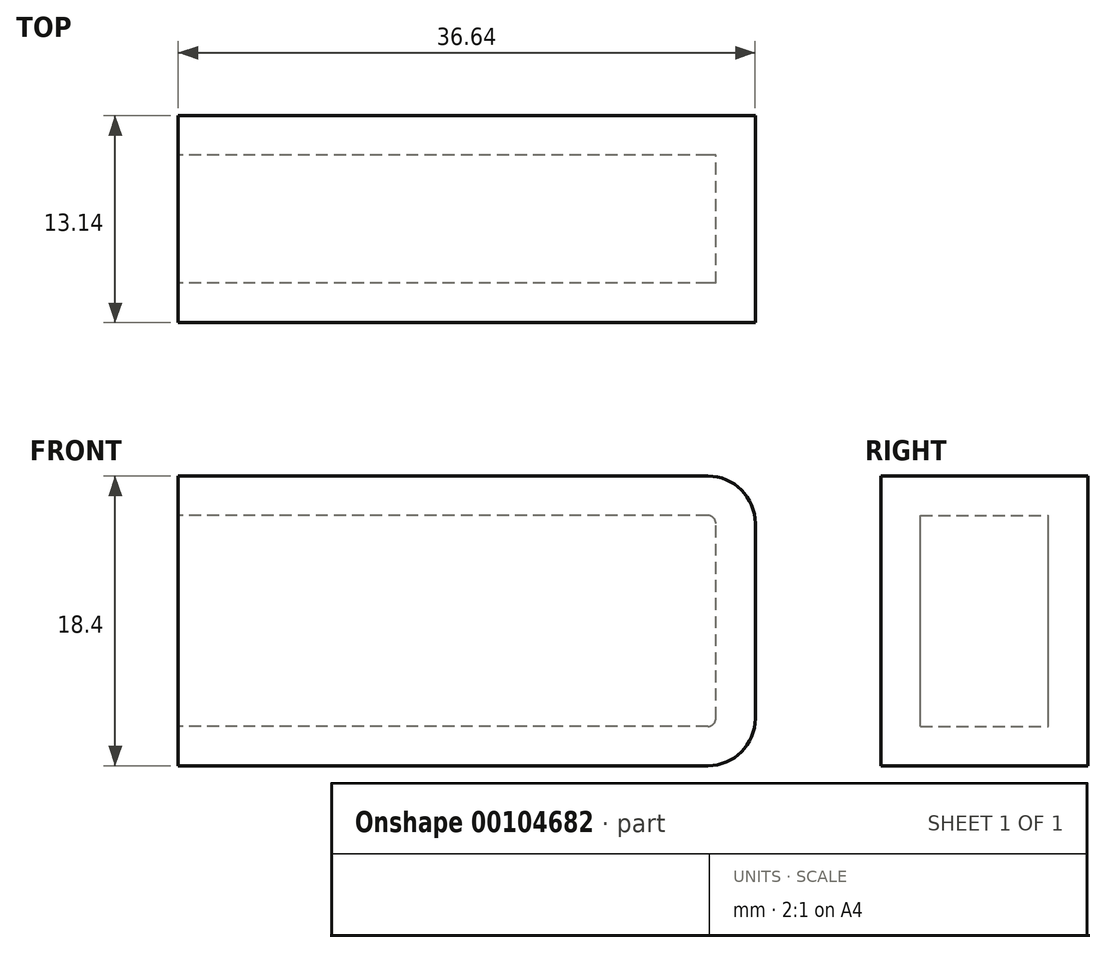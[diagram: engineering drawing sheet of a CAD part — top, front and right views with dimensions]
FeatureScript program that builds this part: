
annotation { "Feature Type Name" : "Feature", "Feature Type Description" : "" }
export const myFeature = defineFeature(function(context is Context, id is Id, definition is map)
    precondition{}
    {
        {
            var Q0;
            Q0=qCreatedBy(makeId("Front.planeOp"),FACE);
            var sketch = newSketch(context, id + "F0", { "sketchPlane" : qUnion([Q0])});
            skLineSegment(sketch, "E0.bottom", {"start": v(15.33, -9.2) * mm, "end": v(-18.32, -9.2) * mm});
            skLineSegment(sketch, "E0.top", {"start": v(15.33, 9.2) * mm, "end": v(-18.32, 9.2) * mm});
            skLineSegment(sketch, "E0.left", {"start": v(18.32, -6.2) * mm, "end": v(18.32, 6.2) * mm});
            skLineSegment(sketch, "E0.right", {"start": v(-18.32, -9.2) * mm, "end": v(-18.32, 9.2) * mm});
            skPoint(sketch, "E0.middle", {"position": v(0, 0) * mm});
            skPoint(sketch, "E1.visualSharp", {"position": v(18.32, 9.2) * mm});
            skArc(sketch, "E1.filletArc", {"start": v(18.32, 6.2) * mm, "mid": v(17.45, 8.32) * mm, "end": v(15.33, 9.2) * mm});
            skPoint(sketch, "E2.visualSharp", {"position": v(18.32, -9.2) * mm});
            skArc(sketch, "E2.filletArc", {"start": v(15.33, -9.2) * mm, "mid": v(17.45, -8.32) * mm, "end": v(18.32, -6.2) * mm});
            skSolve(sketch);
        }
        {
            var Q0;
            Q0=makeQuery(id+"F0.imprint","IMPRINT",FACE,{"disambiguationData":[TD([[makeQuery(id+"F0.imprint","IMPRINT",EDGE,{"derivedFrom":sQuery(id+"F0.wireOp",EDGE,"E0.bottom")}),-1.0]])]});
            extrude(context, id + "F1", {"entities" : qUnion([Q0]), "depth" : (8.14 + 5) * mm});
        }
        {
            var Q0;
            Q0=makeQuery(id+"F1.opExtrude","SWEPT_FACE",FACE,{"disambiguationData":[OSD([sQuery(id+"F0.wireOp",EDGE,"E0.right")])]});
            shell(context, id + "F2", {"entities" : qUnion([Q0]), "thickness" : 2.5 * mm});
        }
    });
